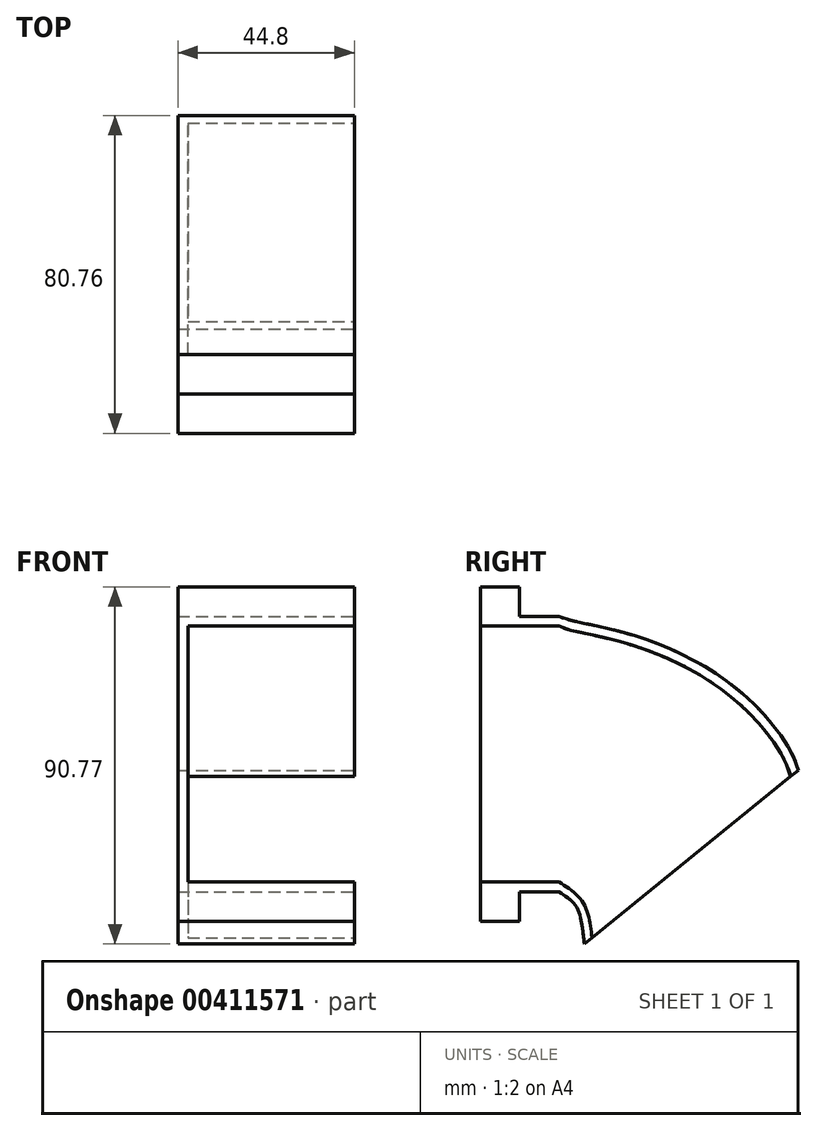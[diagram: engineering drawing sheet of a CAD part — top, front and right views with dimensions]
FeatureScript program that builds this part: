
annotation { "Feature Type Name" : "Feature", "Feature Type Description" : "" }
export const myFeature = defineFeature(function(context is Context, id is Id, definition is map)
    precondition{}
    {
        {
            var Q0;
            Q0=qCreatedBy(makeId("Front.planeOp"),FACE);
            var sketch = newSketch(context, id + "F0", { "sketchPlane" : qUnion([Q0])});
            skLineSegment(sketch, "E0.bottom", {"start": v(-65, 65) * mm, "end": v(0, 65) * mm});
            skLineSegment(sketch, "E0.top", {"start": v(-65, 0) * mm, "end": v(0, 0) * mm});
            skLineSegment(sketch, "E0.left", {"start": v(-65, 65) * mm, "end": v(-65, 0) * mm});
            skLineSegment(sketch, "E0.right", {"start": v(0, 65) * mm, "end": v(0, 0) * mm});
            skLineSegment(sketch, "E1.0", {"start": v(-73, 36.71) * mm, "end": v(-73, -33.29) * mm});
            skLineSegment(sketch, "E2.bottom", {"start": v(10, -10) * mm, "end": v(-75, -10) * mm});
            skLineSegment(sketch, "E2.top", {"start": v(10, 75) * mm, "end": v(-75, 75) * mm});
            skLineSegment(sketch, "E2.left", {"start": v(10, -10) * mm, "end": v(10, 75) * mm});
            skLineSegment(sketch, "E2.right", {"start": v(-75, -10) * mm, "end": v(-75, 75) * mm});
            skSolve(sketch);
        }
        {
            var Q0;
            Q0=makeQuery(id+"F0.imprint","IMPRINT",FACE,{"disambiguationData":[TD([[makeQuery(id+"F0.imprint","IMPRINT",EDGE,{"derivedFrom":sQuery(id+"F0.wireOp",EDGE,"E0.bottom")}),1.0]])]});
            extrude(context, id + "F1", {"entities" : qUnion([Q0]), "depth" : 10 * mm});
        }
        {
            var Q0;
            Q0=qCreatedBy(makeId("Front.planeOp"),FACE);
            var sketch = newSketch(context, id + "F2", { "sketchPlane" : qUnion([Q0])});
            skLineSegment(sketch, "E3.0", {"start": v(-67.5, 67.5) * mm, "end": v(-67.5, -2.5) * mm});
            skLineSegment(sketch, "E3.1", {"start": v(-67.5, 67.5) * mm, "end": v(2.5, 67.5) * mm});
            skLineSegment(sketch, "E3.2", {"start": v(2.5, 67.5) * mm, "end": v(2.5, -2.5) * mm});
            skLineSegment(sketch, "E3.3", {"start": v(-67.5, -2.5) * mm, "end": v(2.5, -2.5) * mm});
            skLineSegment(sketch, "E4.0", {"start": v(0, 65) * mm, "end": v(0, 0) * mm});
            skLineSegment(sketch, "E4.1", {"start": v(-65, 65) * mm, "end": v(0, 65) * mm});
            skLineSegment(sketch, "E4.2", {"start": v(-65, 65) * mm, "end": v(-65, 0) * mm});
            skLineSegment(sketch, "E4.3", {"start": v(-65, 0) * mm, "end": v(0, 0) * mm});
            skSolve(sketch);
        }
        {
            var Q0;
            Q0 = qSketchRegion(id + "F2", true);
            extrude(context, id + "F3", {"entities" : qUnion([Q0]), "operationType" : NewBodyOperationType.ADD, "oppositeDirection" : true, "depth" : 10 * mm});
        }
        {
            var Q0;
            Q0=qCreatedBy(makeId("Right.planeOp"),FACE);
            var sketch = newSketch(context, id + "F4", { "sketchPlane" : qUnion([Q0])});
            skFitSpline(sketch, "E5", {"points": [v(10.18, 0) * mm, v(16.2, -5.2) * mm, v(18.48, -14.33) * mm], "startDerivative": vector(14.54, -9.24) * mm, "endDerivative": vector(2.25, -19.28) * mm});
            skSolve(sketch);
        }
        {
            var Q0;
            Q0=makeQuery(id+"F3.opExtrude","CAP_FACE",FACE,{"disambiguationData":[OSD([sQuery(id+"F2.wireOp",EDGE,"E3.0"),sQuery(id+"F2.wireOp",EDGE,"E3.1"),sQuery(id+"F2.wireOp",EDGE,"E3.2"),sQuery(id+"F2.wireOp",EDGE,"E3.3"),sQuery(id+"F2.wireOp",EDGE,"E4.0"),sQuery(id+"F2.wireOp",EDGE,"E4.1"),sQuery(id+"F2.wireOp",EDGE,"E4.2"),sQuery(id+"F2.wireOp",EDGE,"E4.3")])],"isStart":false});
            var Q1;
            Q1=sQuery(id+"F4.wireOp",EDGE,"E5");
            sweep(context, id + "F5", {"operationType" : NewBodyOperationType.ADD, "profiles" : qUnion([Q0]), "path" : qUnion([Q1])});
        }
        {
            var Q0;
            {var subQ0=sQuery(id+"F2.wireOp",EDGE,"E4.0");Q0=makeQuery(id+"F5.boolean.opBoolean","MERGE",FACE,{"derivedFrom":[makeQuery(id+"F3.boolean.opBoolean","MERGE",FACE,{"derivedFrom":[makeQuery(id+"F1.opExtrude","SWEPT_FACE",FACE,{"disambiguationData":[OSD([sQuery(id+"F0.wireOp",EDGE,"E0.right")])]}),makeQuery(id+"F3.opExtrude","SWEPT_FACE",FACE,{"disambiguationData":[OSD([subQ0])]})]}),makeQuery(id+"F5.opSweep","SWEPT_FACE",FACE,{"disambiguationData":[OSD([subQ0,sQuery(id+"F4.wireOp",EDGE,"E5")])]})]});}
            var sketch = newSketch(context, id + "F6", { "sketchPlane" : qUnion([Q0])});
            skLineSegment(sketch, "E6.bottom", {"start": v(23.8, 82.97) * mm, "end": v(-75.76, 82.97) * mm});
            skLineSegment(sketch, "E6.top", {"start": v(23.8, -28.45) * mm, "end": v(-75.76, -28.45) * mm});
            skLineSegment(sketch, "E6.left", {"start": v(23.8, 82.97) * mm, "end": v(23.8, -28.45) * mm});
            skLineSegment(sketch, "E6.right", {"start": v(-75.76, 82.97) * mm, "end": v(-75.76, -28.45) * mm});
            skSolve(sketch);
        }
        {
            var Q0;
            Q0 = qSketchRegion(id + "F6", true);
            extrude(context, id + "F7", {"entities" : qUnion([Q0]), "operationType" : NewBodyOperationType.REMOVE, "endBound" : BoundingType.SYMMETRIC, "oppositeDirection" : true, "depth" : 45.4 * mm});
        }
        {
            var Q0;
            Q0=makeQuery(id+"F1.opExtrude","SWEPT_FACE",FACE,{"disambiguationData":[OSD([sQuery(id+"F0.wireOp",EDGE,"E2.right")])]});
            var Q1;
            {var subQ0=sQuery(id+"F2.wireOp",EDGE,"E3.0");Q1=makeQuery(id+"F5.boolean.opBoolean","MERGE",FACE,{"derivedFrom":[makeQuery(id+"F3.opExtrude","SWEPT_FACE",FACE,{"disambiguationData":[OSD([subQ0])]}),makeQuery(id+"F5.opSweep","SWEPT_FACE",FACE,{"disambiguationData":[OSD([subQ0,sQuery(id+"F4.wireOp",EDGE,"E5")])]})]});}
            extrude(context, id + "F8", {"entities" : qUnion([Q0]), "operationType" : NewBodyOperationType.REMOVE, "endBound" : BoundingType.UP_TO_SURFACE, "oppositeDirection" : true, "endBoundEntityFace" : qUnion([Q1]), "depth" : 25 * mm});
        }
    });
